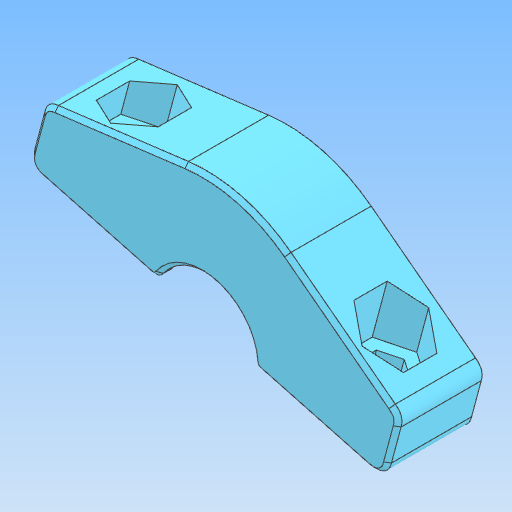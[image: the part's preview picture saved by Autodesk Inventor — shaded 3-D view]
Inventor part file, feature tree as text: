
AUTODESK INVENTOR PART (.ipt)
format: ipt  version: 2021.2 (Build 252289000, 289)  size: 261,632 bytes
history: native  units: mm
features: other x4, fillet x1, chamfer x1
ambient origin geometry x8: Origin, YZ Plane, XZ Plane, XY Plane, X Axis, Y Axis, Z Axis, Center Point
bodies: Body1 (feature_tree)
feature tree (6):
  other  "Твёрдое тело.ipt"
  fillet  "Сопряжение1"  Radius=10.0mm
  chamfer  "Фаска1"  Distance=2.0mm
  other  "Скобка 2::Твёрдое тело.ipt"
  other  "Элемент создания тегов1"
  other  "Твердое тело1"
